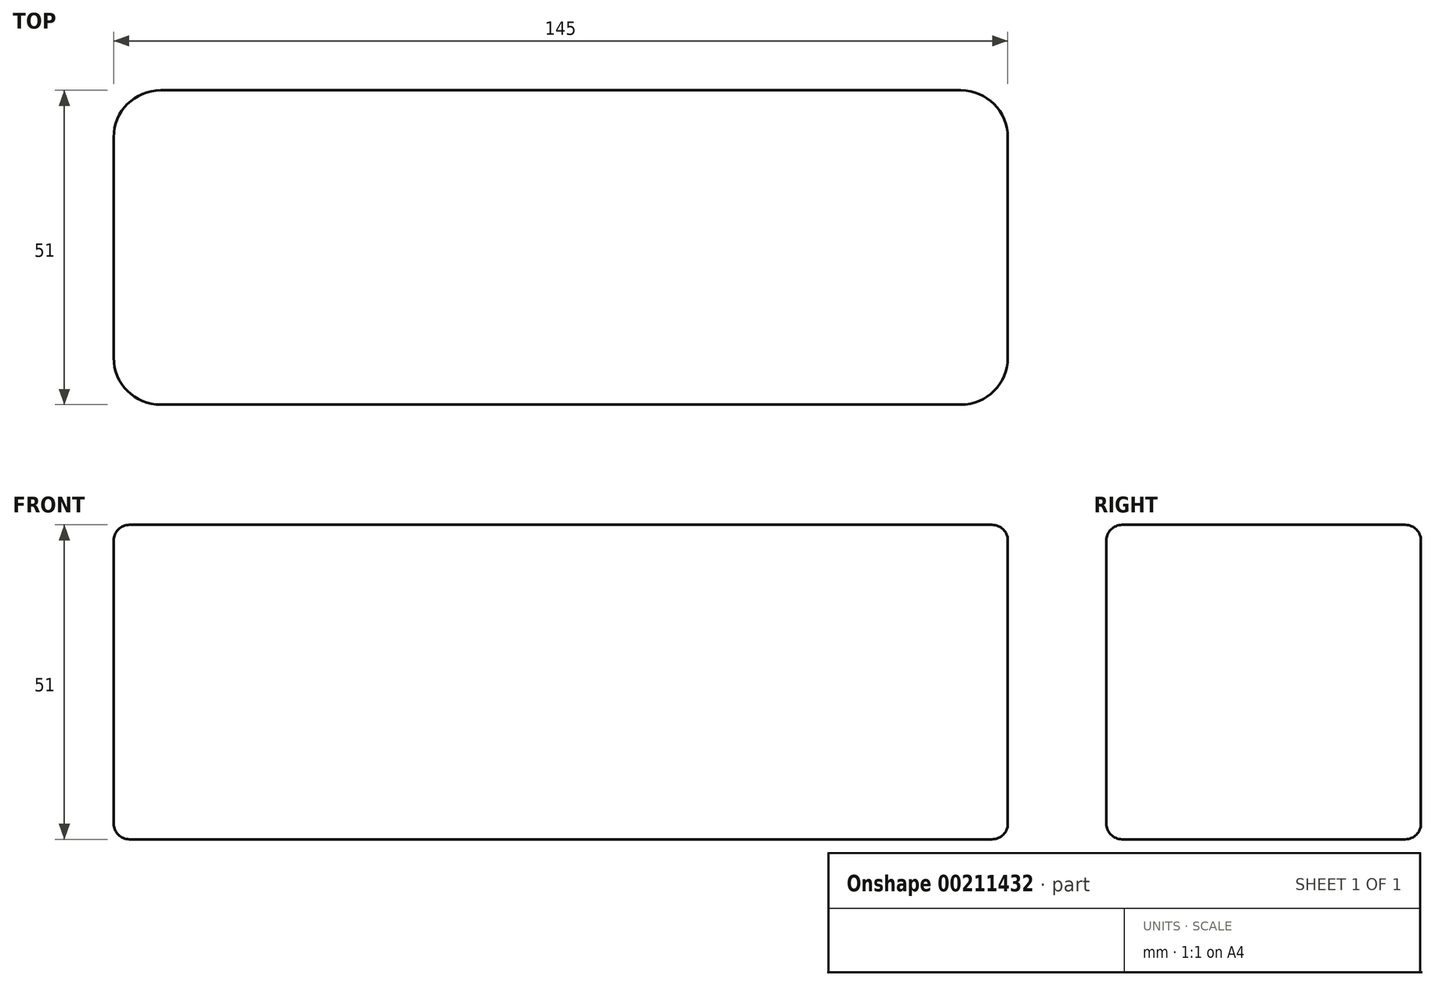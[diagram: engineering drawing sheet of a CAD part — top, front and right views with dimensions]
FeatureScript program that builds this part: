
annotation { "Feature Type Name" : "Feature", "Feature Type Description" : "" }
export const myFeature = defineFeature(function(context is Context, id is Id, definition is map)
    precondition{}
    {
        {
            var Q0;
            Q0=qCreatedBy(makeId("Top.planeOp"),FACE);
            var sketch = newSketch(context, id + "F0", { "sketchPlane" : qUnion([Q0])});
            skLineSegment(sketch, "E0.bottom", {"start": v(-72.5, 25.5) * mm, "end": v(72.5, 25.5) * mm});
            skLineSegment(sketch, "E0.top", {"start": v(-72.5, -25.5) * mm, "end": v(72.5, -25.5) * mm});
            skLineSegment(sketch, "E0.left", {"start": v(-72.5, 25.5) * mm, "end": v(-72.5, -25.5) * mm});
            skLineSegment(sketch, "E0.right", {"start": v(72.5, 25.5) * mm, "end": v(72.5, -25.5) * mm});
            skSolve(sketch);
        }
        {
            var Q0;
            Q0 = qSketchRegion(id + "F0", true);
            extrude(context, id + "F1", {"entities" : qUnion([Q0]), "depth" : 51 * mm});
        }
        {
            var Q0;
            Q0=makeQuery(id+"F1.opExtrude","CAP_EDGE",EDGE,{"disambiguationData":[OSD([sQuery(id+"F0.wireOp",EDGE,"E0.top")])],"isStart":false});
            var Q1;
            Q1=makeQuery(id+"F1.opExtrude","CAP_EDGE",EDGE,{"disambiguationData":[OSD([sQuery(id+"F0.wireOp",EDGE,"E0.bottom")])],"isStart":false});
            var Q2;
            Q2=makeQuery(id+"F1.opExtrude","CAP_EDGE",EDGE,{"disambiguationData":[OSD([sQuery(id+"F0.wireOp",EDGE,"E0.top")])],"isStart":true});
            var Q3;
            Q3=makeQuery(id+"F1.opExtrude","CAP_EDGE",EDGE,{"disambiguationData":[OSD([sQuery(id+"F0.wireOp",EDGE,"E0.bottom")])],"isStart":true});
            var Q4;
            Q4=makeQuery(id+"F1.opExtrude","CAP_EDGE",EDGE,{"disambiguationData":[OSD([sQuery(id+"F0.wireOp",EDGE,"E0.left")])],"isStart":true});
            var Q5;
            Q5=makeQuery(id+"F1.opExtrude","CAP_EDGE",EDGE,{"disambiguationData":[OSD([sQuery(id+"F0.wireOp",EDGE,"E0.left")])],"isStart":false});
            var Q6;
            Q6=makeQuery(id+"F1.opExtrude","CAP_EDGE",EDGE,{"disambiguationData":[OSD([sQuery(id+"F0.wireOp",EDGE,"E0.right")])],"isStart":true});
            var Q7;
            Q7=makeQuery(id+"F1.opExtrude","CAP_EDGE",EDGE,{"disambiguationData":[OSD([sQuery(id+"F0.wireOp",EDGE,"E0.right")])],"isStart":false});
            fillet(context, id + "F2", {"entities" : qUnion([Q0, Q1, Q2, Q3, Q4, Q5, Q6, Q7]), "radius" : 2.54 * mm, "tangentPropagation" : true, "allowEdgeOverflow" : false});
        }
        {
            var Q0;
            Q0=makeQuery(id+"F1.opExtrude","SWEPT_EDGE",EDGE,{"disambiguationData":[OSD([sQuery(id+"F0.wireOp",EDGE,"E0.top"),sQuery(id+"F0.wireOp",EDGE,"E0.right")])]});
            var Q1;
            Q1=makeQuery(id+"F1.opExtrude","SWEPT_EDGE",EDGE,{"disambiguationData":[OSD([sQuery(id+"F0.wireOp",EDGE,"E0.bottom"),sQuery(id+"F0.wireOp",EDGE,"E0.right")])]});
            var Q2;
            Q2=makeQuery(id+"F1.opExtrude","SWEPT_EDGE",EDGE,{"disambiguationData":[OSD([sQuery(id+"F0.wireOp",EDGE,"E0.top"),sQuery(id+"F0.wireOp",EDGE,"E0.left")])]});
            var Q3;
            Q3=makeQuery(id+"F1.opExtrude","SWEPT_EDGE",EDGE,{"disambiguationData":[OSD([sQuery(id+"F0.wireOp",EDGE,"E0.bottom"),sQuery(id+"F0.wireOp",EDGE,"E0.left")])]});
            fillet(context, id + "F3", {"entities" : qUnion([Q0, Q1, Q2, Q3]), "radius" : 7.62 * mm, "tangentPropagation" : true, "allowEdgeOverflow" : false});
        }
    });
